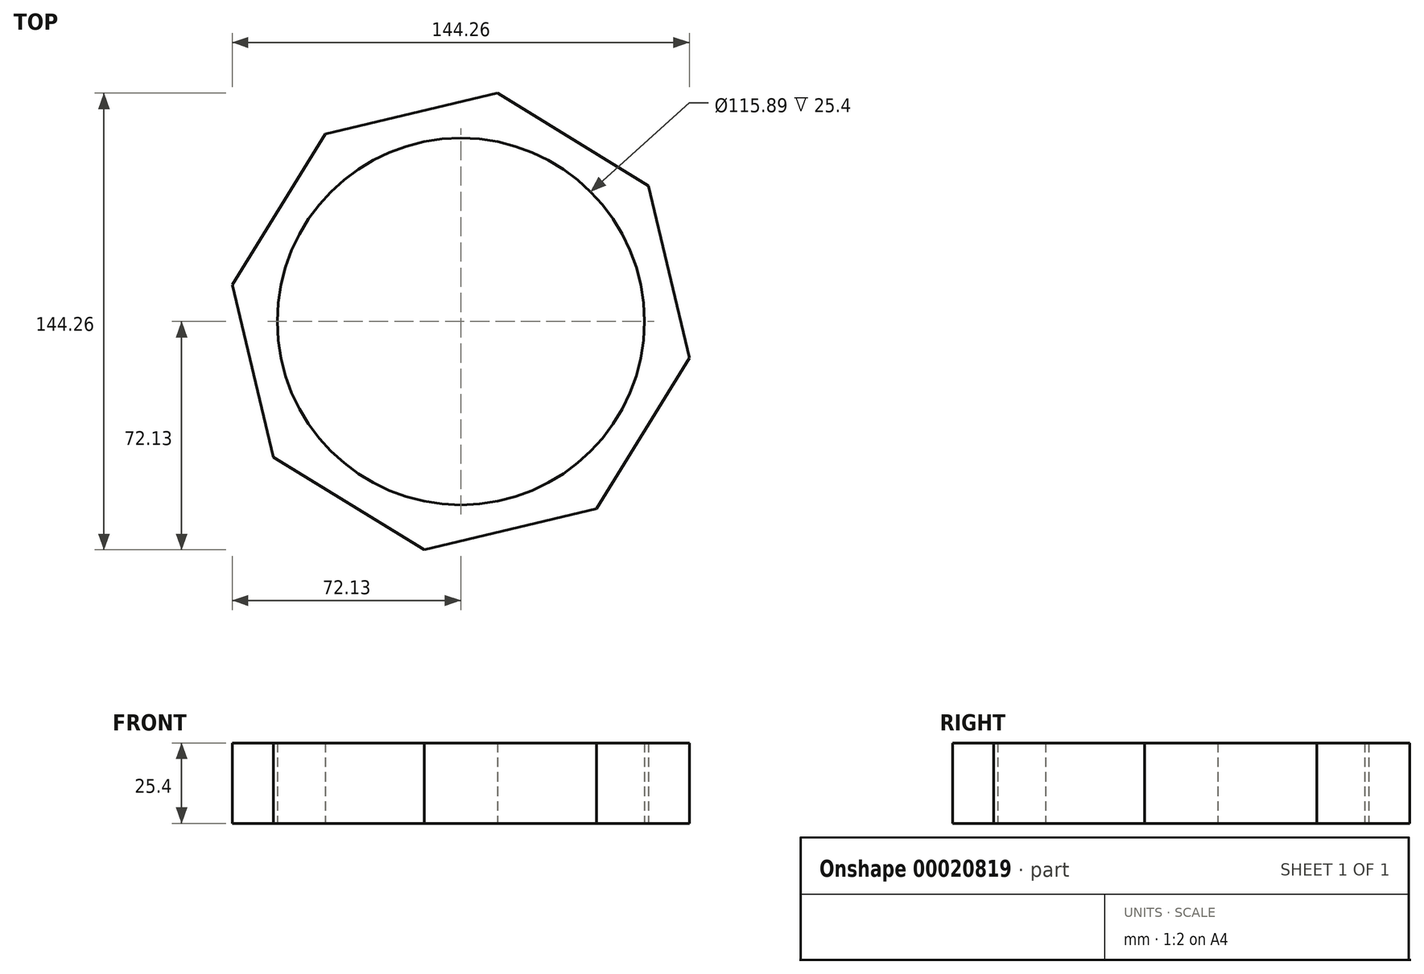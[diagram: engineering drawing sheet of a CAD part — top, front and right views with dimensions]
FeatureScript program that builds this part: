
annotation { "Feature Type Name" : "Feature", "Feature Type Description" : "" }
export const myFeature = defineFeature(function(context is Context, id is Id, definition is map)
    precondition{}
    {
        {
            var Q0;
            Q0=qCreatedBy(makeId("Top.planeOp"),FACE);
            var sketch = newSketch(context, id + "F0", { "sketchPlane" : qUnion([Q0])});
            skCircle(sketch, "E0", {"center": v(0, 0) * mm, "radius": 57.94 * mm});
            skCircle(sketch, "E1.cCircle", {"center": v(0, 0) * mm, "radius": 67.5 * mm, "construction": true});
            skLineSegment(sketch, "E1.0", {"start": v(-11.57, -72.13) * mm, "end": v(-59.19, -42.83) * mm});
            skLineSegment(sketch, "E1.1", {"start": v(-59.19, -42.83) * mm, "end": v(-72.13, 11.57) * mm});
            skLineSegment(sketch, "E1.2", {"start": v(-72.13, 11.57) * mm, "end": v(-42.83, 59.19) * mm});
            skLineSegment(sketch, "E1.3", {"start": v(-42.83, 59.19) * mm, "end": v(11.57, 72.13) * mm});
            skLineSegment(sketch, "E1.4", {"start": v(11.57, 72.13) * mm, "end": v(59.19, 42.83) * mm});
            skLineSegment(sketch, "E1.5", {"start": v(59.19, 42.83) * mm, "end": v(72.13, -11.57) * mm});
            skLineSegment(sketch, "E1.6", {"start": v(72.13, -11.57) * mm, "end": v(42.83, -59.19) * mm});
            skLineSegment(sketch, "E1.7", {"start": v(42.83, -59.19) * mm, "end": v(-11.57, -72.13) * mm});
            skPoint(sketch, "E1.0.midPoint", {"position": v(-35.38, -57.48) * mm});
            skSolve(sketch);
        }
        {
            var Q0;
            Q0=makeQuery(id+"F0.imprint","IMPRINT",FACE,{"disambiguationData":[TD([[makeQuery(id+"F0.imprint","IMPRINT",EDGE,{"derivedFrom":sQuery(id+"F0.wireOp",EDGE,"E0")}),-1.0]])]});
            extrude(context, id + "F1", {"entities" : qUnion([Q0]), "depth" : 25.4 * mm});
        }
    });
